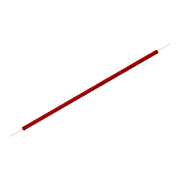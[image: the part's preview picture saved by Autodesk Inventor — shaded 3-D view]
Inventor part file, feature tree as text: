
AUTODESK INVENTOR PART (.ipt)
format: ipt  version: unknown  size: 156,160 bytes
history: native  units: in
note: dims shown in document units (in); Inventor stores cm internally (conversion verified against a paired STEP export)
features: extrude x1, sketch x1
ambient origin geometry x8: Origin, YZ Plane, XZ Plane, XY Plane, X Axis, Y Axis, Z Axis, Center Point
feature tree (2):
  extrude  "Extrusion8"  Depth=1.8898in TaperAngle=0.0deg
  sketch  "Sketch23"  dims[d72=0.0394in d73=1.8898in d74=0.0in]
